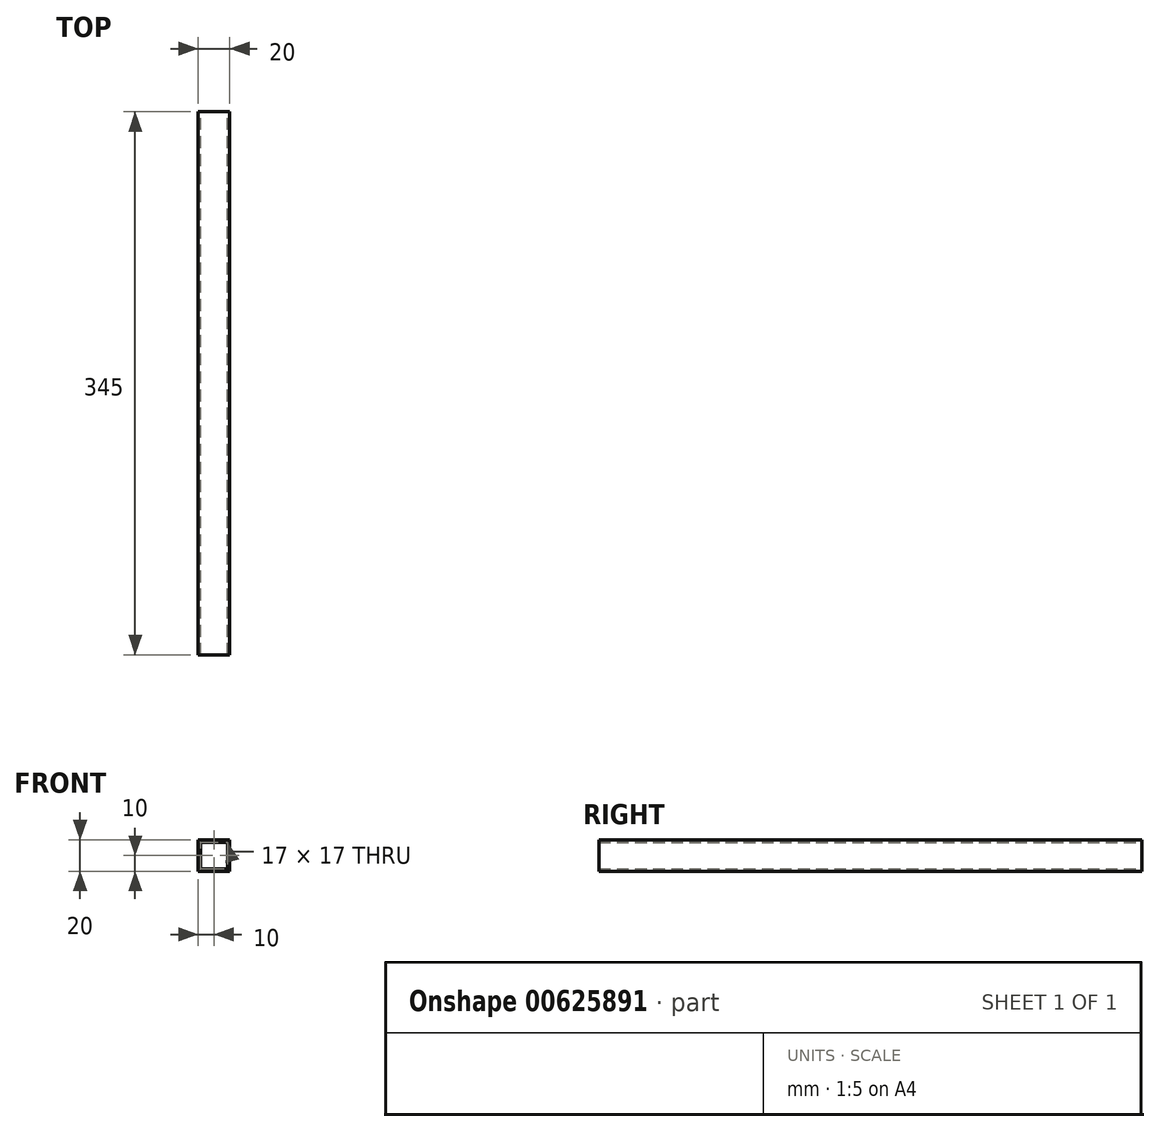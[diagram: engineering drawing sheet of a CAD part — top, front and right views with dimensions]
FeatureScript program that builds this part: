
annotation { "Feature Type Name" : "Feature", "Feature Type Description" : "" }
export const myFeature = defineFeature(function(context is Context, id is Id, definition is map)
    precondition{}
    {
        {
            var Q0;
            Q0=qCreatedBy(makeId("Front.planeOp"),FACE);
            var sketch = newSketch(context, id + "F0", { "sketchPlane" : qUnion([Q0])});
            skLineSegment(sketch, "E0.bottom", {"start": v(0, 0) * mm, "end": v(20, 0) * mm});
            skLineSegment(sketch, "E0.top", {"start": v(0, -20) * mm, "end": v(20, -20) * mm});
            skLineSegment(sketch, "E0.left", {"start": v(0, 0) * mm, "end": v(0, -20) * mm});
            skLineSegment(sketch, "E0.right", {"start": v(20, 0) * mm, "end": v(20, -20) * mm});
            skLineSegment(sketch, "E1.0", {"start": v(1.5, -1.5) * mm, "end": v(18.5, -1.5) * mm});
            skLineSegment(sketch, "E1.1", {"start": v(1.5, -1.5) * mm, "end": v(1.5, -18.5) * mm});
            skLineSegment(sketch, "E1.2", {"start": v(1.5, -18.5) * mm, "end": v(18.5, -18.5) * mm});
            skLineSegment(sketch, "E1.3", {"start": v(18.5, -1.5) * mm, "end": v(18.5, -18.5) * mm});
            skSolve(sketch);
        }
        {
            var Q0;
            Q0=makeQuery(id+"F0.imprint","IMPRINT",FACE,{"disambiguationData":[TD([[makeQuery(id+"F0.imprint","IMPRINT",EDGE,{"derivedFrom":sQuery(id+"F0.wireOp",EDGE,"E0.bottom")}),-1.0]])]});
            extrude(context, id + "F1", {"entities" : qUnion([Q0]), "depth" : 345 * mm, "offsetDistance" : 25 * mm});
        }
    });
